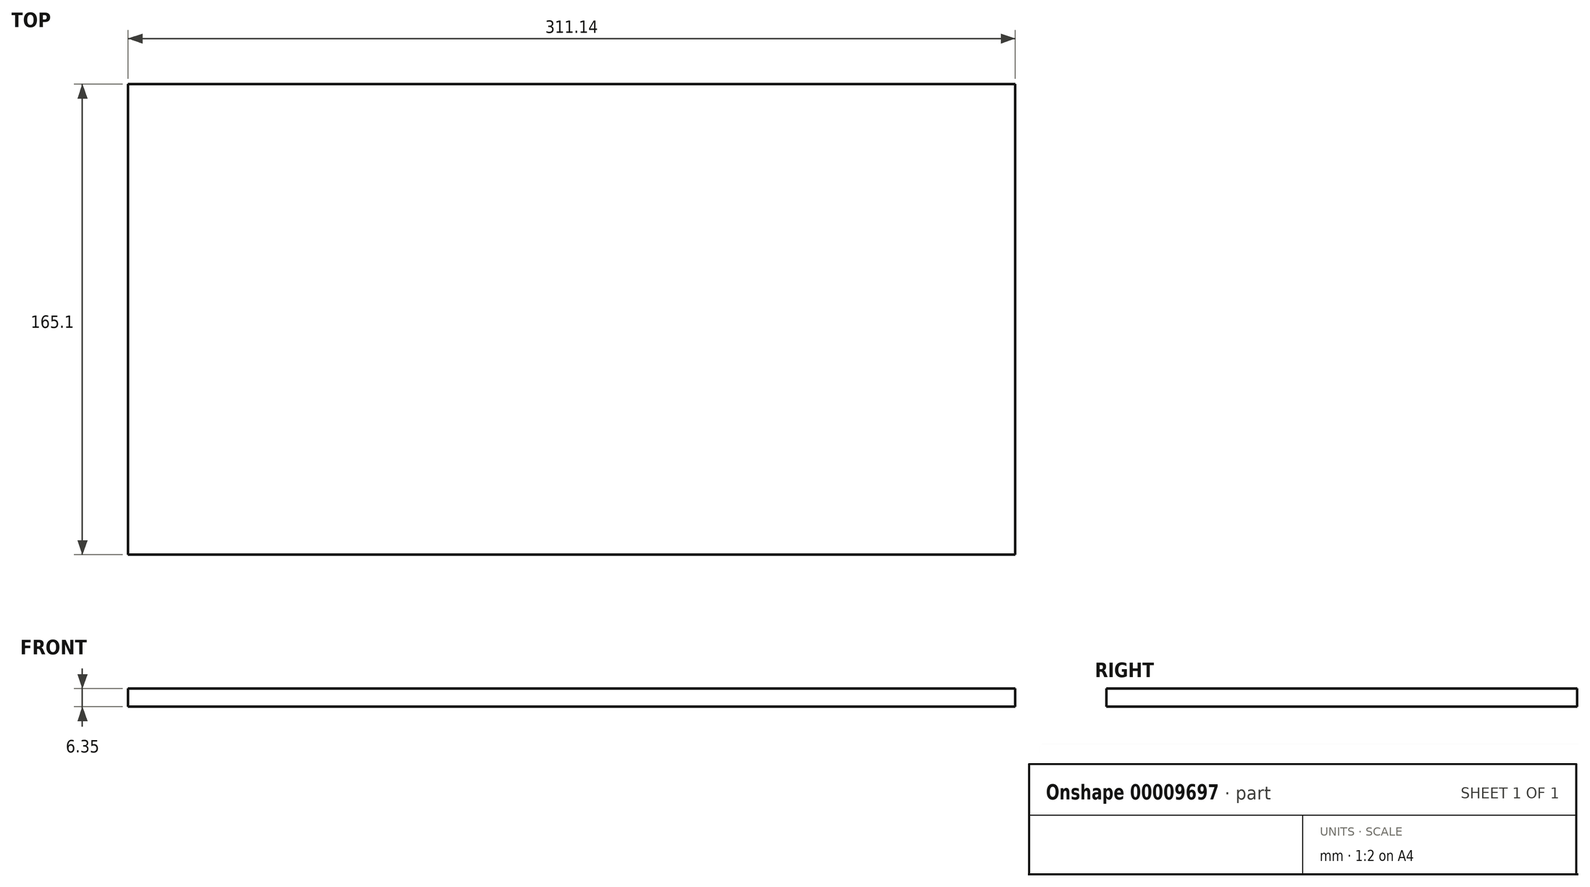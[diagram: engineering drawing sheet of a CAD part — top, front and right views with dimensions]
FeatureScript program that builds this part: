
annotation { "Feature Type Name" : "Feature", "Feature Type Description" : "" }
export const myFeature = defineFeature(function(context is Context, id is Id, definition is map)
    precondition{}
    {
        {
            var Q0;
            Q0=qCreatedBy(makeId("Top.planeOp"),FACE);
            var sketch = newSketch(context, id + "F0", { "sketchPlane" : qUnion([Q0])});
            skLineSegment(sketch, "E0.rect.bottom", {"start": v(155.58, 82.55) * mm, "end": v(-155.58, 82.55) * mm});
            skLineSegment(sketch, "E0.rect.top", {"start": v(155.58, -82.55) * mm, "end": v(-155.58, -82.55) * mm});
            skLineSegment(sketch, "E0.rect.left", {"start": v(155.58, 82.55) * mm, "end": v(155.58, -82.55) * mm});
            skLineSegment(sketch, "E0.rect.right", {"start": v(-155.58, 82.55) * mm, "end": v(-155.58, -82.55) * mm});
            skPoint(sketch, "E0.rect.middle", {"position": v(0, 0) * mm});
            skSolve(sketch);
        }
        {
            var Q0;
            Q0 = qSketchRegion(id + "F0", true);
            extrude(context, id + "F1", {"entities" : qUnion([Q0]), "depth" : 6.35 * mm});
        }
    });
